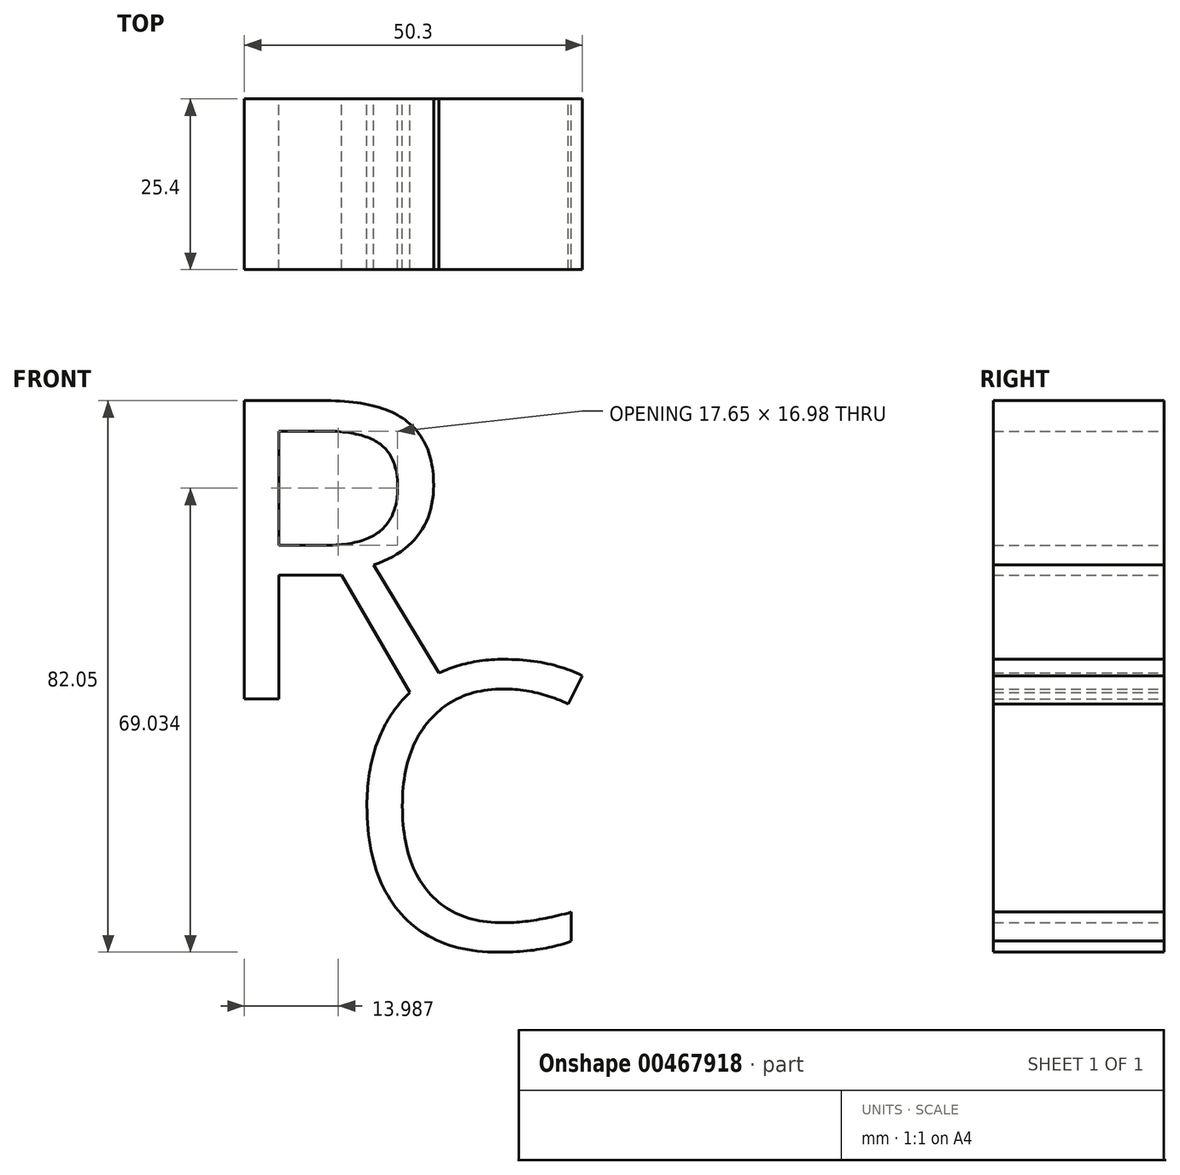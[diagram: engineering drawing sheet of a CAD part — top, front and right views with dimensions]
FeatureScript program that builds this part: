
annotation { "Feature Type Name" : "Feature", "Feature Type Description" : "" }
export const myFeature = defineFeature(function(context is Context, id is Id, definition is map)
    precondition{}
    {
        {
            var Q0;
            Q0=qCreatedBy(makeId("Front.planeOp"),FACE);
            var sketch = newSketch(context, id + "F0", { "sketchPlane" : qUnion([Q0])});
            skText(sketch, "E0", { "text": "R", "fontName": "OpenSans-Regular.ttf"});
            skText(sketch, "E1", { "text": "C", "fontName": "OpenSans-Regular.ttf"});
            const initialGuessF0  = {"E0": [-0.03447, -0.01568, 1, 0, 0.04478], "E1": [-0.01376, -0.05275, 1, 0, 0.04275]};
            skSetInitialGuess(sketch, initialGuessF0);
            skSolve(sketch);
        }
        {
            var Q0;
            Q0 = qSketchRegion(id + "F0", true);
            extrude(context, id + "F1", {"entities" : qUnion([Q0]), "depth" : 25.4 * mm});
        }
    });
